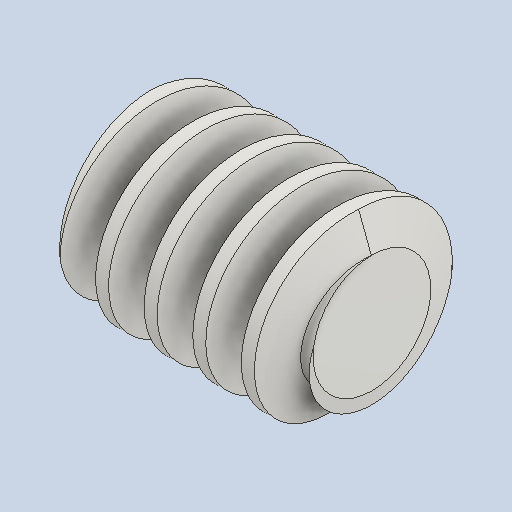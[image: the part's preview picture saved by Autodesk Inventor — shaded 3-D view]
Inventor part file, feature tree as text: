
AUTODESK INVENTOR PART (.ipt)
format: ipt  version: 2024 (Build 280153000, 153)  size: 284,672 bytes
history: native  units: mm (DEFAULTED — no unit token found)
features: other x6, chamfer x2, pattern_circular x2, extrude x1
ambient origin geometry x6: Origin, XZ Plane, X Axis, Y Axis, Z Axis, Center Point
bodies: Solid1 (feature_tree)
feature tree (11):
  extrude  "Base Body"  Depth=40.0mm
  chamfer  "Chamfer1"  Distance=48.0mm
  chamfer  "Chamfer2"  Distance=60.0mm
  other  "Tooth Sketch"
  other  "Tooth"
  pattern_circular  "Tooth Pattern"  [2 undecoded]
  other  "Left Tooth"
  pattern_circular  "Left Tooth Pattern"  [2 undecoded]
  other  "Base Body Sketch"
  other  "Srf1"
  other  "Pitch Diameter"
note: 4 required parameter values undecoded (feature->parameter linkage not recoverable at this tier; creation-order binding heuristic only, values carry confidence <= 0.55)
